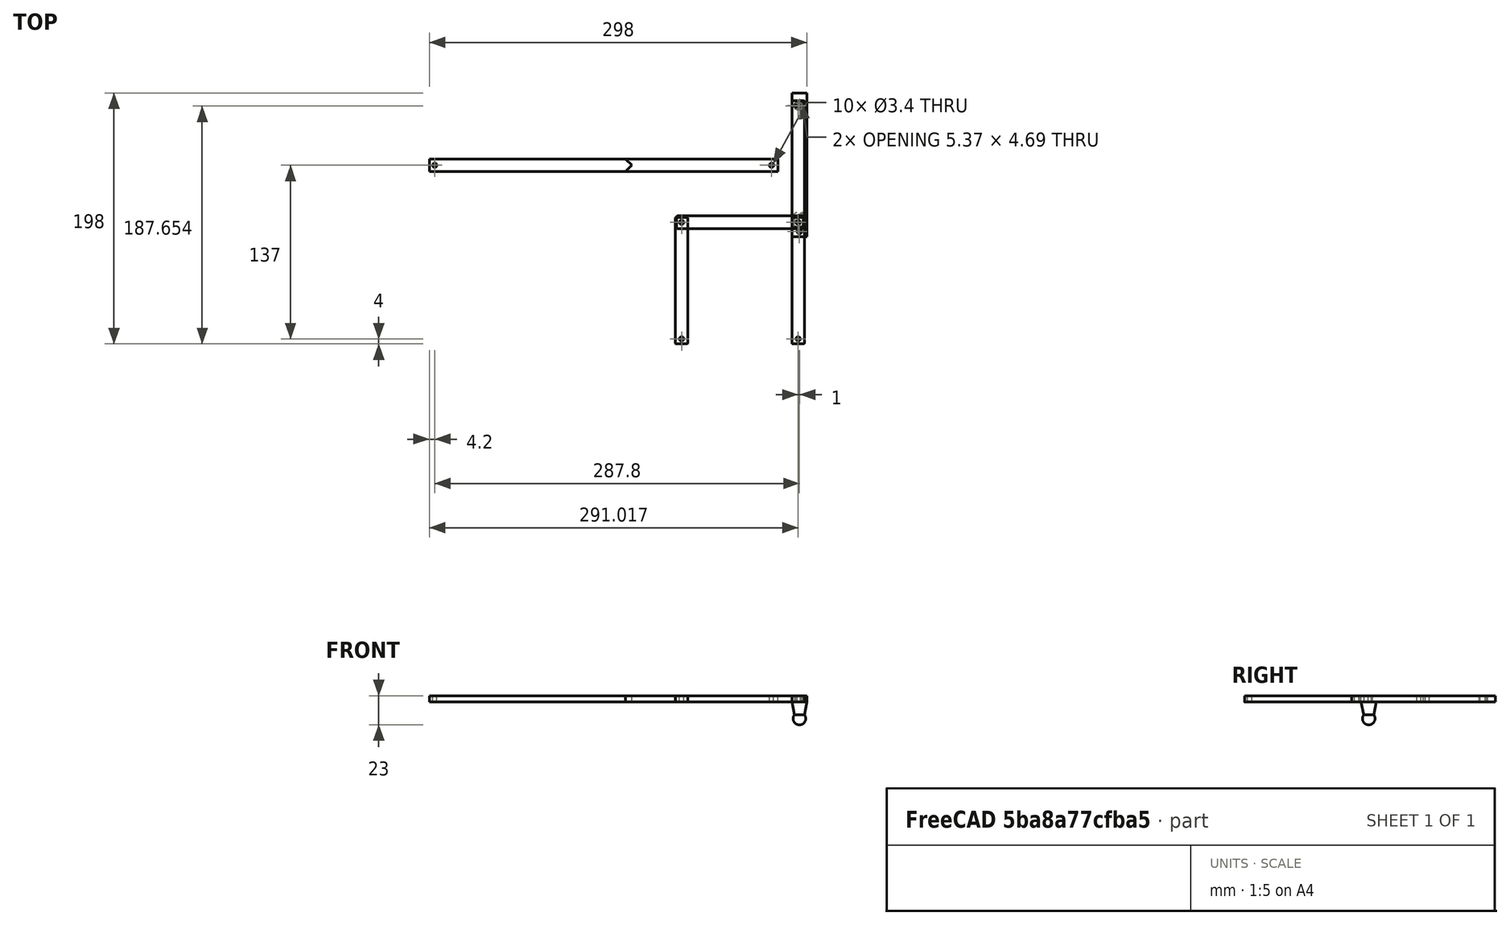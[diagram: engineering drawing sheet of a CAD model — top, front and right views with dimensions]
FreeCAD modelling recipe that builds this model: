
FCSTD DOCUMENT  (FreeCAD 0.14R3702 (Git))
Label: Square
License: CC-BY 3.0
LicenseURL: http://creativecommons.org/licenses/by/3.0/
objects: Part::Fillet×12, Part::Cut×10, Part::Box×8, Part::Cylinder×7, Part::Fuse×2, Part::MultiCommon×1, Part::Cone×1, Part::Sphere×1
note: 42 computed .brp shape members not serialized (recipe doc carries the construction recipe); baked Part::Feature solids carry a one-line shape summary decoded from their .brp

FEATURE [Part::Box] Box  label="Cube"
  Height = 5
  Length = 100
  Width = 10
FEATURE [Part::Cylinder] Cylinder
  Angle = 360
  Height = 10
  Placement = pos=(4,5,-1) rot=(0,0,1;0rad)
  Radius = 1.7
FEATURE [Part::Cylinder] Cylinder001
  Angle = 360
  Height = 10
  Placement = pos=(96,5,-2) rot=(0,0,1;0rad)
  Radius = 1.7
FEATURE [Part::Cut] Cut
  Base = -> Box
  Tool = -> Cylinder
FEATURE [Part::Cut] Cut001
  Base = -> Cut
  Tool = -> Cylinder001
FEATURE [Part::Fillet] Fillet
  Base = -> Cut001
  Edges = 1 edges r=1: [Edge13]
FEATURE [Part::Fillet] Fillet001
  Base = -> Fillet
  Edges = 1 edges r=1: [Edge15]
FEATURE [Part::Fillet] Fillet002
  Base = -> Fillet001
  Edges = 1 edges r=1: [Edge17]
FEATURE [Part::Fillet] Fillet003
  Base = -> Fillet002
  Edges = 1 edges r=1: [Edge17]
FEATURE [Part::Fillet] Fillet005
  Base = -> Fillet001
  Edges = 1 edges r=1: [Edge17]
FEATURE [Part::Fillet] Fillet004
  Base = -> Fillet005
  Edges = 1 edges r=1: [Edge17]
  Placement = pos=(-1,9,0) rot=(0,0,-1;1.5708rad)
FEATURE [Part::Fillet] Fillet007
  Base = -> Fillet001
  Edges = 1 edges r=1: [Edge17]
FEATURE [Part::Fillet] Fillet006
  Base = -> Fillet007
  Edges = 1 edges r=1: [Edge17]
  Placement = pos=(101,-91,0) rot=(0,0,1;1.5708rad)
FEATURE [Part::Fillet] Fillet009
  Base = -> Fillet001
  Edges = 1 edges r=1: [Edge17]
FEATURE [Part::Fillet] Fillet008
  Base = -> Fillet009
  Edges = 1 edges r=1: [Edge17]
  Placement = pos=(101,1,0) rot=(0,0,1;1.5708rad)
FEATURE [Part::Cylinder] Cylinder002
  Angle = 360
  Height = 10
  Placement = pos=(96,97,-3) rot=(0,0,1;0rad)
  Radius = 2.7
FEATURE [Part::Box] Box001  label="Cube001"
  Height = 10
  Length = 10
  Placement = pos=(90.8,99,-3) rot=(0,0,1;0rad)
  Width = 10
FEATURE [Part::Cut] Cut002
  Base = -> Cylinder002
  Tool = -> Box001
FEATURE [Part::Cut] Cut003
  Base = -> Fillet008
  Tool = -> Cut002
FEATURE [Part::Fillet] Fillet011
  Base = -> Fillet001
  Edges = 1 edges r=1: [Edge17]
FEATURE [Part::Fillet] Fillet010
  Base = -> Fillet011
  Edges = 1 edges r=1: [Edge17]
  Placement = pos=(-1,9,0) rot=(0,0,-1;1.5708rad)
FEATURE [Part::Box] Box002  label="Cube002"
  Height = 5
  Length = 275
  Placement = pos=(-195,45,0) rot=(0,0,1;0rad)
  Width = 10
FEATURE [Part::Cylinder] Cylinder003
  Angle = 360
  Height = 10
  Placement = pos=(-190.8,50,-2) rot=(0,0,1;0rad)
  Radius = 1.7
FEATURE [Part::Cylinder] Cylinder004
  Angle = 360
  Height = 10
  Placement = pos=(75,50,-2) rot=(0,0,1;0rad)
  Radius = 1.7
FEATURE [Part::Box] Box003  label="Cube003"
  Height = 10
  Length = 400
  Placement = pos=(-601,50,-3) rot=(0,0,-1;0.785398rad)
  Width = 400
FEATURE [Part::Box] Box004  label="Cube004"
  Height = 5
  Length = 275
  Placement = pos=(-195,45,0) rot=(0,0,1;0rad)
  Width = 10
FEATURE [Part::Cut] Cut004
  Base = -> Box004
  Tool = -> Box003
FEATURE [Part::Box] Box005  label="Cube005"
  Height = 10
  Length = 400
  Placement = pos=(-601,50,-3) rot=(0,0,-1;0.785398rad)
  Width = 400
FEATURE [Part::MultiCommon] Common
  Shapes = -> [Box002,Box005]
FEATURE [Part::Cut] Cut005  label="Long arm part a"
  Base = -> Cut004
  Tool = -> Cylinder004
FEATURE [Part::Cut] Cut006  label="long arm part b"
  Base = -> Common
  Tool = -> Cylinder003
FEATURE [Part::Box] Box006  label="Cube006"
  Height = 5
  Length = 12
  Placement = pos=(91,-5,0) rot=(0,0,1;0rad)
  Width = 113.4
FEATURE [Part::Cylinder] Cylinder005
  Angle = 360
  Height = 10
  Placement = pos=(97,97,-3) rot=(0,0,1;0rad)
  Radius = 2.7
FEATURE [Part::Box] Box007  label="Cube007"
  Height = 10
  Length = 10
  Placement = pos=(91.8,99,-3) rot=(0,0,1;0rad)
  Width = 10
FEATURE [Part::Cut] Cut007
  Base = -> Cylinder005
  Placement = pos=(0,2,0) rot=(0,0,1;0rad)
  Tool = -> Box007
FEATURE [Part::Cut] Cut008
  Base = -> Box006
  Placement = pos=(0,-1.4,0) rot=(0,0,1;0rad)
  Tool = -> Cut007
FEATURE [Part::Cylinder] Cylinder006
  Angle = 360
  Height = 10
  Placement = pos=(97,-2.4,-1) rot=(0,0,1;0rad)
  Radius = 1.7
FEATURE [Part::Cut] Cut009
  Base = -> Cut008
  Tool = -> Cylinder006
FEATURE [Part::Cone] Cone
  Angle = 360
  Height = 10
  Placement = pos=(97,7,-10) rot=(0,0,1;0rad)
  Radius1 = 4
  Radius2 = 6
FEATURE [Part::Sphere] Sphere
  Angle1 = -90
  Angle2 = 90
  Angle3 = 360
  Placement = pos=(97,7,-13) rot=(0,0,1;0rad)
  Radius = 5
FEATURE [Part::Fuse] Fusion
  Base = -> Cut009
  Tool = -> Cone
FEATURE [Part::Fuse] Fusion001
  Base = -> Sphere
  Tool = -> Fusion
